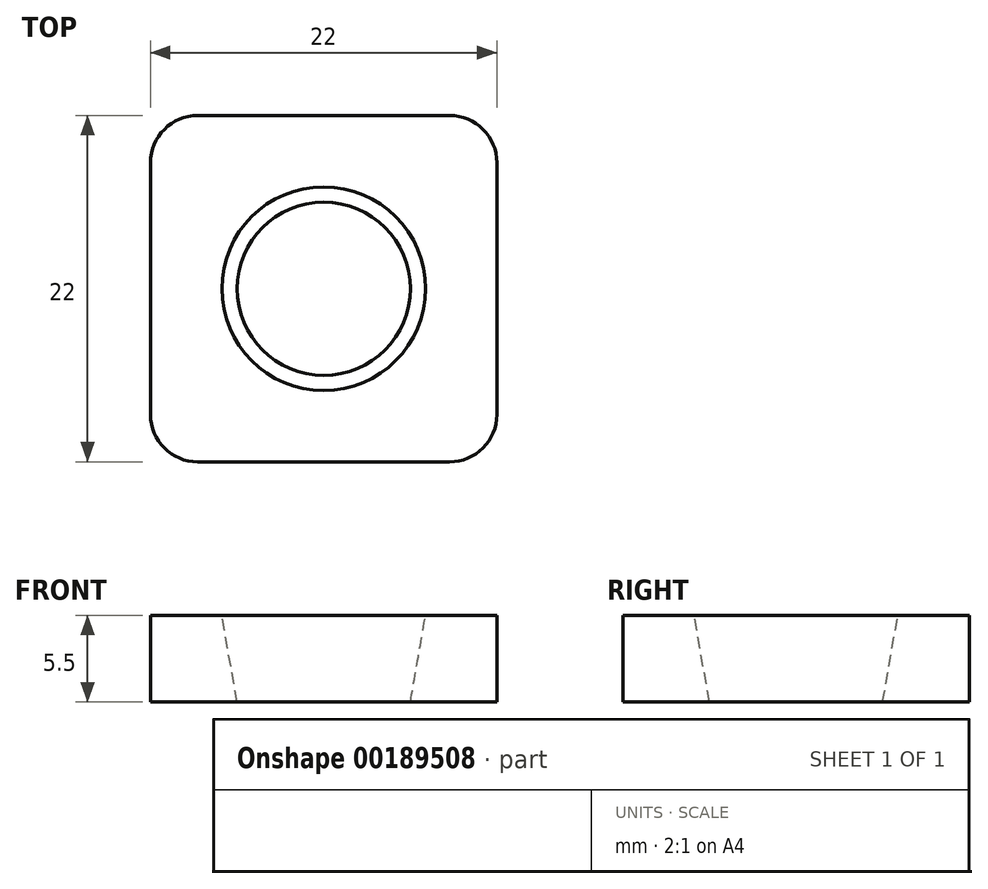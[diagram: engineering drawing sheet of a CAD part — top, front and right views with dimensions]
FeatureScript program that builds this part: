
annotation { "Feature Type Name" : "Feature", "Feature Type Description" : "" }
export const myFeature = defineFeature(function(context is Context, id is Id, definition is map)
    precondition{}
    {
        {
            assignVariable(context, id + "F0", {"name" : "tool_hook_h", "anyValue" : 5.5});
        }
        {
            assignVariable(context, id + "F1", {"name" : "tool_hook_fillet_r", "anyValue" : 3});
        }
        {
            assignVariable(context, id + "F2", {"name" : "tool_hole_draft_angle", "anyValue" : 10});
        }
        {
            var Q0;
            Q0=qCreatedBy(makeId("Top.planeOp"),FACE);
            var sketch = newSketch(context, id + "F3", { "sketchPlane" : qUnion([Q0])});
            skLineSegment(sketch, "E0.bottom", {"start": v(11, -11) * mm, "end": v(-11, -11) * mm});
            skLineSegment(sketch, "E0.top", {"start": v(11, 11) * mm, "end": v(-11, 11) * mm});
            skLineSegment(sketch, "E0.left", {"start": v(11, -11) * mm, "end": v(11, 11) * mm});
            skLineSegment(sketch, "E0.right", {"start": v(-11, -11) * mm, "end": v(-11, 11) * mm});
            skPoint(sketch, "E0.middle", {"position": v(0, 0) * mm});
            skSolve(sketch);
        }
        {
            var Q0;
            Q0 = qSketchRegion(id + "F3", true);
            extrude(context, id + "F4", {"entities" : qUnion([Q0]), "depth" : (getVariable(context, 'tool_hook_h')) * mm});
        }
        {
            var Q0;
            Q0=makeQuery(id+"F4.opExtrude","SWEPT_EDGE",EDGE,{"disambiguationData":[OSD([sQuery(id+"F3.wireOp",EDGE,"E0.bottom"),sQuery(id+"F3.wireOp",EDGE,"E0.left")])]});
            var Q1;
            Q1=makeQuery(id+"F4.opExtrude","SWEPT_EDGE",EDGE,{"disambiguationData":[OSD([sQuery(id+"F3.wireOp",EDGE,"E0.top"),sQuery(id+"F3.wireOp",EDGE,"E0.left")])]});
            var Q2;
            Q2=makeQuery(id+"F4.opExtrude","SWEPT_EDGE",EDGE,{"disambiguationData":[OSD([sQuery(id+"F3.wireOp",EDGE,"E0.top"),sQuery(id+"F3.wireOp",EDGE,"E0.right")])]});
            var Q3;
            Q3=makeQuery(id+"F4.opExtrude","SWEPT_EDGE",EDGE,{"disambiguationData":[OSD([sQuery(id+"F3.wireOp",EDGE,"E0.bottom"),sQuery(id+"F3.wireOp",EDGE,"E0.right")])]});
            fillet(context, id + "F5", {"entities" : qUnion([Q0, Q1, Q2, Q3]), "radius" : (getVariable(context, 'tool_hook_fillet_r')) * mm, "tangentPropagation" : true, "allowEdgeOverflow" : false});
        }
        {
            var Q0;
            Q0=makeQuery(id+"F4.opExtrude","CAP_FACE",FACE,{"disambiguationData":[OSD([sQuery(id+"F3.wireOp",EDGE,"E0.bottom"),sQuery(id+"F3.wireOp",EDGE,"E0.top"),sQuery(id+"F3.wireOp",EDGE,"E0.left"),sQuery(id+"F3.wireOp",EDGE,"E0.right")])],"isStart":true});
            var sketch = newSketch(context, id + "F6", { "sketchPlane" : qUnion([Q0])});
            skCircle(sketch, "E1", {"center": v(0, 0) * mm, "radius": 5.5 * mm});
            skSolve(sketch);
        }
        {
            var Q0;
            Q0 = qSketchRegion(id + "F6", true);
            var Q1;
            Q1=makeQuery(id+"F4.opExtrude","CAP_FACE",FACE,{"disambiguationData":[OSD([sQuery(id+"F3.wireOp",EDGE,"E0.bottom"),sQuery(id+"F3.wireOp",EDGE,"E0.top"),sQuery(id+"F3.wireOp",EDGE,"E0.left"),sQuery(id+"F3.wireOp",EDGE,"E0.right")])],"isStart":false});
            extrude(context, id + "F7", {"entities" : qUnion([Q0]), "operationType" : NewBodyOperationType.REMOVE, "endBound" : BoundingType.UP_TO_SURFACE, "oppositeDirection" : true, "endBoundEntityFace" : qUnion([Q1]), "depth" : 25 * mm, "hasDraft" : true, "draftAngle" : (getVariable(context, 'tool_hole_draft_angle')) * degree});
        }
    });
